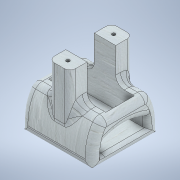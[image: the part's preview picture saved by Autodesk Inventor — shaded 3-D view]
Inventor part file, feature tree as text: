
AUTODESK INVENTOR PART (.ipt)
format: ipt  version: 2021 (Build 250183000, 183)  size: 948,736 bytes
history: native  units: mm
features: extrude x23, sketch x23, fillet x7, projected_geometry x6, plane x1, mirror x1
ambient origin geometry x8: Origin, YZ Plane, XZ Plane, XY Plane, X Axis, Y Axis, Z Axis, Center Point
bodies: Solid1 (feature_tree)
feature tree (61):
  extrude  "Extrusion1"  Depth=39.0mm
  extrude  "Extrusion2"  Depth=8.0mm
  plane  "Work Plane2"
  mirror  "Mirror1"
  extrude  "Extrusion3"  Depth=8.0mm
  extrude  "Extrusion4"  Depth=4.0mm TaperAngle=0.0deg
  extrude  "Extrusion5"  Depth=10.0mm
  extrude  "Extrusion6"  Depth=4.0mm TaperAngle=0.0deg
  extrude  "Extrusion7"  Depth=19.0mm
  extrude  "Extrusion8"  Depth=4.0mm TaperAngle=0.0deg
  extrude  "Extrusion9"  Depth=4.0mm TaperAngle=0.0deg
  extrude  "Extrusion10"  Depth=2.0mm TaperAngle=0.0deg
  extrude  "Extrusion11"  Depth=12.5mm
  extrude  "Extrusion12"  Depth=4.0mm
  extrude  "Extrusion13"  Depth=7.9mm
  extrude  "Extrusion14"  Depth=7.9mm
  extrude  "Extrusion15"  Depth=6.0mm TaperAngle=0.0deg
  extrude  "Extrusion16"  Depth=8.5mm TaperAngle=0.0deg
  extrude  "Extrusion17"  Depth=8.5mm TaperAngle=0.0deg
  fillet  "Fillet6"  Radius=36.0mm
  fillet  "Fillet7"  Radius=8.5mm
  fillet  "Fillet8"  Radius=15.0mm
  extrude  "Extrusion18"  Depth=6.0mm
  fillet  "Fillet9"  Radius=6.0mm
  extrude  "Extrusion20"  Depth=8.5mm TaperAngle=0.0deg
  extrude  "Extrusion21"  Depth=7.9mm
  extrude  "Extrusion22"  Depth=7.9mm
  extrude  "Extrusion23"  Depth=11.0mm
  fillet  "Fillet14"  Radius=11.0mm
  fillet  "Fillet15"  Radius=11.0mm
  fillet  "Fillet16"  Radius=11.0mm
  extrude  "Extrusion24"  Depth=11.0mm
  sketch  "Sketch1"  dims[d0=15.0mm d1=39.0mm]
  sketch  "Sketch2"  dims[d2=4.0mm d3=0.0mm d5=8.0mm]
  sketch  "Sketch3"  dims[d6=15.0mm d7=8.0mm]
  sketch  "Sketch4"  dims[d8=14.0mm d9=4.0mm d10=0.0mm]
  sketch  "Sketch5"  dims[d12=10.0mm d13=27.0mm]
  sketch  "Sketch7"  dims[d14=28.0mm d15=4.0mm d16=0.0mm]
  sketch  "Sketch8"  dims[d17=28.0mm d18=19.0mm]
  sketch  "Sketch10"  dims[d19=4.0mm d20=0.0mm d21=4.0mm d22=0.0mm]
  projected_geometry  "Projected Loop2"
  sketch  "Sketch11"  dims[d23=13.0mm d24=0.0mm d25=4.0mm d26=0.0mm]
  projected_geometry  "Projected Loop3"
  sketch  "Sketch12"  dims[d27=3.0mm d28=0.0mm d29=2.0mm d30=0.0mm]
  projected_geometry  "Projected Loop4"
  sketch  "Sketch14"  dims[d31=2.0mm d32=0.0mm d35=12.5mm]
  sketch  "Sketch15"  dims[d36=11.5mm d37=4.0mm]
  sketch  "Sketch18"  dims[d38=6.0mm d39=7.9mm]
  sketch  "Sketch19"  dims[d40=7.9mm d41=7.9mm]
  projected_geometry  "Projected Loop9"
  sketch  "Sketch20"  dims[d42=7.9mm d43=6.0mm d44=0.0mm]
  projected_geometry  "Projected Loop10"
  sketch  "Sketch21"  dims[d45=0.2mm d46=0.0mm d49=8.5mm d50=56.5mm d51=0.0mm d52=0.0mm]
  sketch  "Sketch22"  dims[d53=8.5mm d54=0.0mm d55=8.5mm d56=0.0mm d57=36.0mm d58=8.5mm d59=0.0mm d61=15.0mm d62=0.0mm]
  sketch  "Sketch23"  dims[d63=4.0mm d64=6.0mm d65=6.0mm]
  projected_geometry  "Projected Loop12"
  sketch  "Sketch25"  dims[d66=30.0mm d70=8.5mm d71=0.0mm]
  sketch  "Sketch26"  dims[d72=3.0mm d79=7.9mm]
  sketch  "Sketch27"  dims[d80=7.9mm d81=7.9mm]
  sketch  "Sketch28"  dims[d82=7.9mm d83=11.0mm d84=11.0mm d85=11.0mm d86=11.0mm]
  sketch  "Sketch29"  dims[d88=11.0mm d89=11.0mm d90=11.0mm d91=11.0mm d92=2.4mm d93=2.4mm d94=15.0mm d95=0.0mm d96=21.0mm d97=2.2mm d98=0.0mm d99=6.0mm d101=2.2mm d102=0.0mm d103=15.0mm d104=0.0mm d105=5.0mm d106=5.0mm d107=5.0mm d108=6.5mm d109=15.0mm d110=0.0mm]
